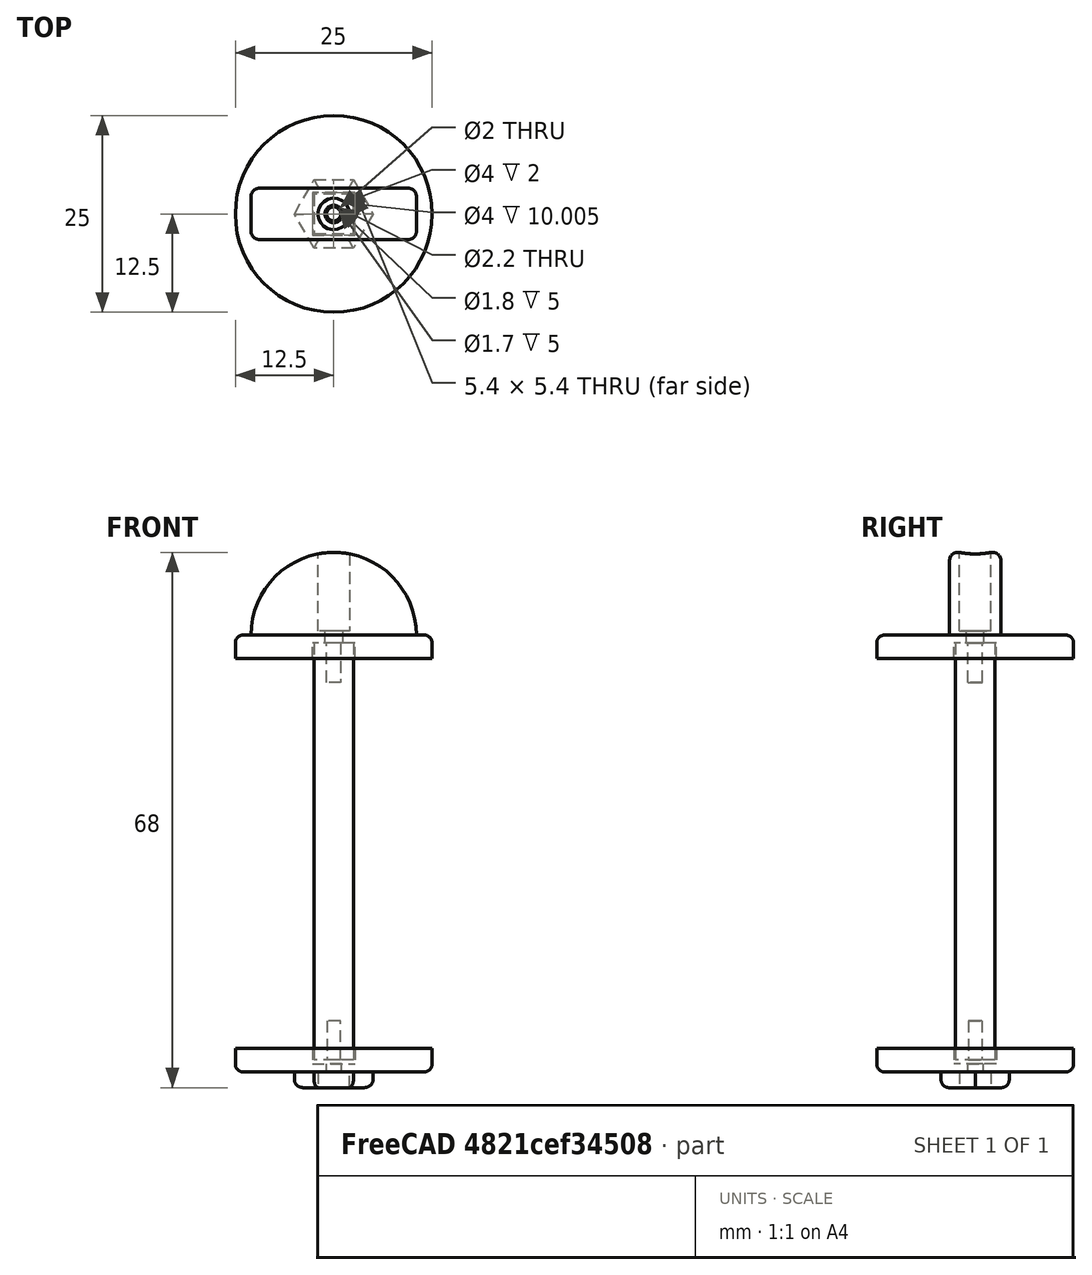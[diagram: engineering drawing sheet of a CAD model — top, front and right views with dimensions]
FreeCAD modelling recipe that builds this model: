
FCSTD DOCUMENT  (FreeCAD 1.0R39109 (Git))
Label: SimpleDoorLock
License: All rights reserved
LicenseURL: http://en.wikipedia.org/wiki/All_rights_reserved
objects: Sketcher::SketchObject×13, PartDesign::Pocket×8, PartDesign::Pad×5, PartDesign::Body×3, Mesh::Feature×3, PartDesign::Fillet×2
note: 74 computed .brp shape members not serialized (recipe doc carries the construction recipe); baked Part::Feature solids carry a one-line shape summary decoded from their .brp

FEATURE [Sketcher::SketchObject] Sketch  label="FlareSketch"
  ArcFitTolerance = 0
  AttachmentSupport = -> [XY_Plane]
  FullyConstrained = true
  MakeInternals = false
  MapMode = 5
  sketch-geometry (1):
    g0: Circle CenterX=0 CenterY=0 CenterZ=0 NormalX=0 NormalY=0 NormalZ=1 AngleXU=0 Radius=12.5
  constraints (2):
    c: Coincident(g0,g-1)
    c: Diameter(g0) = 25  'padDiameter'
FEATURE [PartDesign::Pad] Pad  label="FlarePad"
  Direction = (0,0,1)
  Length = 3
  Length2 = 10
  Profile = -> Sketch
  ReferenceAxis = -> Sketch [N_Axis]
  Reversed = true
  Suppressed = false
  Type = 0
FEATURE [Sketcher::SketchObject] Sketch002  label="HandleSketch"
  ArcFitTolerance = 0
  AttachmentSupport = -> [XZ_Plane]
  ExternalGeometry = -> [Pad]
  FullyConstrained = true
  MakeInternals = false
  MapMode = 5
  Placement = pos=(0,0,0) rot=(1,0,0;1.5708rad)
  sketch-geometry (3):
    g0: GeomPoint [constr] X=10.5 Y=0 Z=0
    g1: ArcOfCircle CenterX=1e-16 CenterY=0 CenterZ=0 NormalX=0 NormalY=0 NormalZ=1 AngleXU=0 Radius=10.5 StartAngle=1.953e-13 EndAngle=3.14159
    g2: LineSegment StartX=-10.5 StartY=5.37603e-11 StartZ=0 EndX=10.5 EndY=5.37603e-11 EndZ=0
  constraints (8):
    c: Coincident(g1,g-1)
    c: PointOnObject(g0,g-3)
    c: DistanceX(g0,g-3) = 2
    c: PointOnObject(g0,g1)
    c: PointOnObject(g1,g-3)
    c: Coincident(g2,g1)
    c: Coincident(g2,g1)
    c: Horizontal(g2)
FEATURE [PartDesign::Pad] Pad001  label="HandlePad"
  BaseFeature = -> Pad
  Direction = (0,-1,2e-16)
  Length = 6.5
  Length2 = 10
  Midplane = true
  Profile = -> Sketch002
  ReferenceAxis = -> Sketch002 [N_Axis]
  Suppressed = false
  Type = 0
FEATURE [Sketcher::SketchObject] Sketch003  label="SkrewHoleSketch"
  ArcFitTolerance = 0
  AttachmentSupport = -> [XY_Plane]
  FullyConstrained = true
  MakeInternals = false
  MapMode = 5
  sketch-geometry (1):
    g0: Circle CenterX=0 CenterY=0 CenterZ=0 NormalX=0 NormalY=0 NormalZ=1 AngleXU=0 Radius=1.1
  constraints (2):
    c: Coincident(g0,g-1)
    c: Diameter(g0) = 2.2
FEATURE [PartDesign::Pocket] Pocket  label="SkrewHolePocket"
  BaseFeature = -> Pad001
  Direction = (0,0,-1)
  Length = 5
  Length2 = 5
  Midplane = true
  Profile = -> Sketch003
  ReferenceAxis = -> Sketch003 [N_Axis]
  Suppressed = false
  Type = 1
FEATURE [Sketcher::SketchObject] Sketch004  label="SkrewHeadSketch"
  ArcFitTolerance = 0
  AttachmentOffset = pos=(0,0,16.5) rot=(0,0,1;0rad)
  AttachmentSupport = -> [XY_Plane]
  FullyConstrained = true
  MakeInternals = false
  MapMode = 5
  Placement = pos=(0,0,16.5) rot=(0,0,1;0rad)
  sketch-geometry (1):
    g0: Circle CenterX=0 CenterY=0 CenterZ=0 NormalX=0 NormalY=0 NormalZ=1 AngleXU=0 Radius=2
  constraints (2):
    c: Coincident(g0,g-1)
    c: Diameter(g0) = 4
FEATURE [PartDesign::Pocket] Pocket001  label="SkrewHeadPocket"
  BaseFeature = -> Pocket
  Direction = (0,0,-1)
  Length = 16
  Length2 = 5
  Profile = -> Sketch004
  ReferenceAxis = -> Sketch004 [N_Axis]
  Suppressed = false
  Type = 0
FEATURE [Sketcher::SketchObject] Sketch005  label="KeyAttachementSketch"
  ArcFitTolerance = 0
  AttachmentSupport = -> [Pocket001]
  FullyConstrained = true
  MakeInternals = false
  MapMode = 5
  Placement = pos=(0,0,-3) rot=(1,0,0;3.14159rad)
  sketch-geometry (5):
    g0: LineSegment StartX=-2.7 StartY=2.7 StartZ=0 EndX=-2.7 EndY=-2.7 EndZ=0
    g1: LineSegment StartX=-2.7 StartY=-2.7 StartZ=0 EndX=2.7 EndY=-2.7 EndZ=0
    g2: LineSegment StartX=2.7 StartY=-2.7 StartZ=0 EndX=2.7 EndY=2.7 EndZ=0
    g3: LineSegment StartX=2.7 StartY=2.7 StartZ=0 EndX=-2.7 EndY=2.7 EndZ=0
    g4: GeomPoint [constr] X=0 Y=0 Z=0
  constraints (12):
    c: Coincident(g0,g1)
    c: Coincident(g1,g2)
    c: Coincident(g2,g3)
    c: Coincident(g3,g0)
    c: Horizontal(g1)
    c: Horizontal(g3)
    c: Vertical(g0)
    c: Vertical(g2)
    c: Symmetric(g1,g0,g4)
    c: Coincident(g4,g-1)
    c: DistanceX(g3,g3) = 5.4
    c: DistanceY(g2,g2) = 5.4
FEATURE [PartDesign::Pocket] Pocket002  label="KeyAttachementPocket"
  BaseFeature = -> Pocket001
  Direction = (0,0,1)
  Length = 2
  Length2 = 5
  Profile = -> Sketch005
  ReferenceAxis = -> Sketch005 [N_Axis]
  Suppressed = false
  Type = 0
FEATURE [Sketcher::SketchObject] Sketch006  label="BaseKeySketch"
  ArcFitTolerance = 0
  AttachmentOffset = pos=(0,0,-1) rot=(0,0,1;0rad)
  AttachmentSupport = -> [XY_Plane001]
  FullyConstrained = true
  MakeInternals = false
  MapMode = 5
  Placement = pos=(0,0,-1) rot=(0,0,1;0rad)
  sketch-geometry (5):
    g0: LineSegment StartX=-2.5 StartY=2.5 StartZ=0 EndX=-2.5 EndY=-2.5 EndZ=0
    g1: LineSegment StartX=-2.5 StartY=-2.5 StartZ=0 EndX=2.5 EndY=-2.5 EndZ=0
    g2: LineSegment StartX=2.5 StartY=-2.5 StartZ=0 EndX=2.5 EndY=2.5 EndZ=0
    g3: LineSegment StartX=2.5 StartY=2.5 StartZ=0 EndX=-2.5 EndY=2.5 EndZ=0
    g4: GeomPoint [constr] X=0 Y=0 Z=0
  constraints (12):
    c: Coincident(g0,g1)
    c: Coincident(g1,g2)
    c: Coincident(g2,g3)
    c: Coincident(g3,g0)
    c: Horizontal(g1)
    c: Horizontal(g3)
    c: Vertical(g0)
    c: Vertical(g2)
    c: Symmetric(g1,g0,g4)
    c: Coincident(g4,g-1)
    c: DistanceX(g3,g3) = 5
    c: DistanceY(g2,g2) = 5
FEATURE [PartDesign::Pad] Pad002  label="BaseKeyPad"
  Direction = (0,0,1)
  Length = 53
  Length2 = 10
  Profile = -> Sketch006
  ReferenceAxis = -> Sketch006 [N_Axis]
  Reversed = true
  Suppressed = false
  Type = 0
FEATURE [Sketcher::SketchObject] Sketch007  label="TopSelfTappingSketch"
  ArcFitTolerance = 0
  AttachmentSupport = -> [Pad002]
  FullyConstrained = true
  MakeInternals = false
  MapMode = 5
  Placement = pos=(0,0,-1) rot=(0,0,1;0rad)
  sketch-geometry (1):
    g0: Circle CenterX=0 CenterY=0 CenterZ=0 NormalX=0 NormalY=0 NormalZ=1 AngleXU=0 Radius=0.9
  constraints (2):
    c: Coincident(g0,g-1)
    c: Diameter(g0) = 1.8  'selfTappingHoleDia'
FEATURE [PartDesign::Pocket] Pocket003  label="TopSelfTappyingPocket"
  BaseFeature = -> Pad002
  Direction = (0,0,-1)
  Length = 5
  Length2 = 5
  Profile = -> Sketch007
  ReferenceAxis = -> Sketch007 [N_Axis]
  Suppressed = false
  Type = 0
FEATURE [PartDesign::Fillet] Fillet
  Base = -> Pocket002 [Edge13,Edge12,Edge2]
  BaseFeature = -> Pocket002
  Radius = 1
  SupportTransform = false
  Suppressed = false
  UseAllEdges = false
FEATURE [PartDesign::Body] Body  label="Controller"
  AllowCompound = false
  Group = -> [Sketch,Pad,Sketch002,Pad001,Sketch003,Pocket,Sketch004,Pocket001,Sketch005,Pocket002,Fillet]
  Origin = -> Origin
  Tip = -> Fillet
FEATURE [Sketcher::SketchObject] Sketch009  label="BottomSelfTappingSketch"
  ArcFitTolerance = 0
  AttachmentSupport = -> [Pocket003]
  FullyConstrained = true
  MakeInternals = false
  MapMode = 5
  Placement = pos=(0,0,-54) rot=(1,0,0;3.14159rad)
  sketch-geometry (1):
    g0: Circle CenterX=0 CenterY=0 CenterZ=0 NormalX=0 NormalY=0 NormalZ=1 AngleXU=0 Radius=0.85
  constraints (2):
    c: Coincident(g0,g-1)
    c: Diameter(g0) = 1.7
FEATURE [PartDesign::Pocket] Pocket004  label="BottomSelfTappingPocket"
  BaseFeature = -> Pocket003
  Direction = (0,0,1)
  Length = 5
  Length2 = 5
  Profile = -> Sketch009
  ReferenceAxis = -> Sketch009 [N_Axis]
  Suppressed = false
  Type = 0
FEATURE [PartDesign::Body] Body001  label="Key"
  AllowCompound = false
  Group = -> [Sketch006,Pad002,Sketch007,Pocket003,Sketch009,Pocket004]
  Origin = -> Origin001
  Tip = -> Pocket004
FEATURE [Sketcher::SketchObject] Sketch010  label="BackFlareSketch"
  ArcFitTolerance = 0
  AttachmentOffset = pos=(0,0,-54) rot=(0,0,1;0rad)
  AttachmentSupport = -> [XY_Plane002]
  FullyConstrained = true
  MakeInternals = false
  MapMode = 5
  Placement = pos=(0,0,-54) rot=(0,0,1;0rad)
  expr: Constraints[1] = <<FlareSketch>>.Constraints.padDiameter
  sketch-geometry (1):
    g0: Circle CenterX=0 CenterY=0 CenterZ=0 NormalX=0 NormalY=0 NormalZ=1 AngleXU=0 Radius=12.5
  constraints (2):
    c: Coincident(g0,g-1)
    c: Diameter(g0) = 25
FEATURE [PartDesign::Pad] Pad003  label="BackFlarePadding"
  Direction = (0,0,1)
  Length = 3
  Length2 = 10
  Midplane = true
  Profile = -> Sketch010
  ReferenceAxis = -> Sketch010 [N_Axis]
  Suppressed = false
  Type = 0
FEATURE [Sketcher::SketchObject] Sketch011  label="KeyAttachmentSketch"
  ArcFitTolerance = 0
  AttachmentSupport = -> [Pad003]
  FullyConstrained = true
  MakeInternals = false
  MapMode = 5
  Placement = pos=(0,0,-52.5) rot=(0,0,1;0rad)
  sketch-geometry (5):
    g0: LineSegment StartX=-2.7 StartY=2.7 StartZ=0 EndX=-2.7 EndY=-2.7 EndZ=0
    g1: LineSegment StartX=-2.7 StartY=-2.7 StartZ=0 EndX=2.7 EndY=-2.7 EndZ=0
    g2: LineSegment StartX=2.7 StartY=-2.7 StartZ=0 EndX=2.7 EndY=2.7 EndZ=0
    g3: LineSegment StartX=2.7 StartY=2.7 StartZ=0 EndX=-2.7 EndY=2.7 EndZ=0
    g4: GeomPoint [constr] X=0 Y=0 Z=0
  constraints (12):
    c: Coincident(g0,g1)
    c: Coincident(g1,g2)
    c: Coincident(g2,g3)
    c: Coincident(g3,g0)
    c: Horizontal(g1)
    c: Horizontal(g3)
    c: Vertical(g0)
    c: Vertical(g2)
    c: Symmetric(g1,g0,g4)
    c: Coincident(g4,g-1)
    c: DistanceX(g3,g3) = 5.4
    c: DistanceY(g2,g2) = 5.4
FEATURE [PartDesign::Pocket] Pocket005  label="KeyAttachementPocket001"
  BaseFeature = -> Pad003
  Direction = (0,0,-1)
  Length = 2
  Length2 = 5
  Profile = -> Sketch011
  ReferenceAxis = -> Sketch011 [N_Axis]
  Suppressed = false
  Type = 0
FEATURE [Sketcher::SketchObject] Sketch014  label="SkrewBulbSketch"
  ArcFitTolerance = 0
  FullyConstrained = true
  MakeInternals = false
  MapMode = 5
  Placement = pos=(0,0,-55.5) rot=(1,0,0;3.14159rad)
  sketch-geometry (7):
    g0: LineSegment StartX=5 StartY=0 StartZ=0 EndX=2.5 EndY=4.33013 EndZ=0
    g1: LineSegment StartX=2.5 StartY=4.33013 StartZ=0 EndX=-2.5 EndY=4.33013 EndZ=0
    g2: LineSegment StartX=-2.5 StartY=4.33013 StartZ=0 EndX=-5 EndY=4.778e-13 EndZ=0
    g3: LineSegment StartX=-5 StartY=4.778e-13 StartZ=0 EndX=-2.5 EndY=-4.33013 EndZ=0
    g4: LineSegment StartX=-2.5 StartY=-4.33013 StartZ=0 EndX=2.5 EndY=-4.33013 EndZ=0
    g5: LineSegment StartX=2.5 StartY=-4.33013 StartZ=0 EndX=5 EndY=0 EndZ=0
    g6: Circle [constr] CenterX=0 CenterY=0 CenterZ=0 NormalX=0 NormalY=0 NormalZ=1 AngleXU=0 Radius=5
  constraints (16):
    c: Coincident(g0,g1)
    c: Coincident(g1,g2)
    c: Coincident(g2,g3)
    c: Coincident(g3,g4)
    c: Coincident(g4,g5)
    c: Coincident(g5,g0)
    c: Equal(g0, g1-g5) x5
    c: PointOnObject(g0,g6)
    c: PointOnObject(g1,g6)
    c: PointOnObject(g2,g6)
    c: PointOnObject(g3,g6)
    c: PointOnObject(g4,g6)
    c: PointOnObject(g5,g6)
    c: Coincident(g6,g-1)
    c: PointOnObject(g5,g-1)
    c: Diameter(g6) = 10
FEATURE [PartDesign::Pad] Pad004  label="SkrewBulbPadding"
  BaseFeature = -> Pocket005
  Direction = (0,-1e-16,-1)
  Length = 2
  Length2 = 10
  Profile = -> Sketch014
  ReferenceAxis = -> Sketch014 [N_Axis]
  Suppressed = false
  Type = 0
FEATURE [Sketcher::SketchObject] Sketch015  label="SkrewSketch"
  ArcFitTolerance = 0
  AttachmentSupport = -> [Pad004]
  FullyConstrained = true
  MakeInternals = false
  MapMode = 5
  Placement = pos=(0,0,-57.5) rot=(1,0,0;3.14159rad)
  sketch-geometry (1):
    g0: Circle CenterX=0 CenterY=0 CenterZ=0 NormalX=0 NormalY=0 NormalZ=1 AngleXU=0 Radius=1
  constraints (2):
    c: Coincident(g0,g-1)
    c: Diameter(g0) = 2
FEATURE [PartDesign::Pocket] Pocket006  label="SkrewPocket"
  BaseFeature = -> Pad004
  Direction = (0,0,1)
  Length = 5
  Length2 = 5
  Profile = -> Sketch015
  ReferenceAxis = -> Sketch015 [N_Axis]
  Suppressed = false
  Type = 1
FEATURE [Sketcher::SketchObject] Sketch016  label="SkrewBrimSketch"
  ArcFitTolerance = 0
  AttachmentSupport = -> [Pocket006]
  FullyConstrained = true
  MakeInternals = false
  MapMode = 5
  Placement = pos=(0,0,-57.5) rot=(1,0,0;3.14159rad)
  sketch-geometry (1):
    g0: Circle CenterX=0 CenterY=0 CenterZ=0 NormalX=0 NormalY=0 NormalZ=1 AngleXU=0 Radius=2
  constraints (2):
    c: Coincident(g0,g-1)
    c: Diameter(g0) = 4
FEATURE [PartDesign::Pocket] Pocket007  label="SkrewBrimPocket"
  BaseFeature = -> Pocket006
  Direction = (0,0,1)
  Length = 2
  Length2 = 5
  Profile = -> Sketch016
  ReferenceAxis = -> Sketch016 [N_Axis]
  Suppressed = false
  Type = 0
FEATURE [PartDesign::Fillet] Fillet001  label="Backfillet"
  Base = -> Pocket007 [Edge2,Edge18,Edge16,Edge25,Edge24,Edge22,Edge20]
  BaseFeature = -> Pocket007
  Radius = 1
  SupportTransform = false
  Suppressed = false
  UseAllEdges = false
FEATURE [PartDesign::Body] Body002  label="Back"
  AllowCompound = false
  Group = -> [Sketch010,Pad003,Sketch011,Pocket005,Sketch014,Pad004,Sketch015,Pocket006,Sketch016,Pocket007,Fillet001]
  Origin = -> Origin002
  Tip = -> Fillet001
FEATURE [Mesh::Feature] Mesh  label="Controller (Meshed)"
FEATURE [Mesh::Feature] Mesh001  label="Key (Meshed)"
FEATURE [Mesh::Feature] Mesh002  label="Back (Meshed)"
